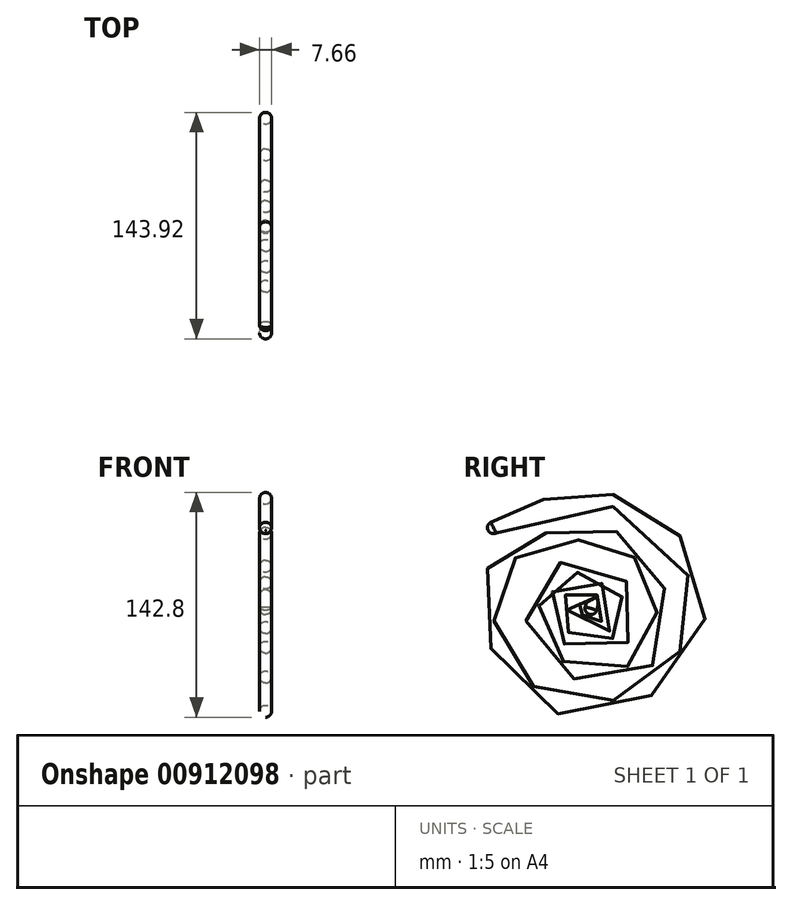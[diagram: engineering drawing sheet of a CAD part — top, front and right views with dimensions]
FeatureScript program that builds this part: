
annotation { "Feature Type Name" : "Feature", "Feature Type Description" : "" }
export const myFeature = defineFeature(function(context is Context, id is Id, definition is map)
    precondition{}
    {
        {
            var Q0;
            Q0=qCreatedBy(makeId("Right.planeOp"),FACE);
            var sketch = newSketch(context, id + "F0", { "sketchPlane" : qUnion([Q0])});
            skFitSpline(sketch, "E0", {"points": [v(-61.4, 46.77) * mm, v(-21.75, 63.7) * mm, v(40.37, 56.93) * mm, v(70.1, -19.46) * mm, v(-17.16, -65.63) * mm, v(-62.36, 11.24) * mm, v(-20.3, 42.18) * mm, v(33.84, 32.75) * mm, v(42.06, -34.45) * mm, v(-23.45, -33.72) * mm, v(-23.2, 18) * mm, v(23.45, 11.97) * mm, v(22, -23.8) * mm, v(-18.13, -15.83) * mm, v(-13.05, 10.27) * mm, v(11.36, 7.61) * mm, v(14.26, -13.42) * mm, v(-6.04, -7.61) * mm, v(-4.1, 4.71) * mm, v(3.87, 2.78) * mm, v(2.66, -6.4) * mm], "startDerivative": vector(711, 380.87) * mm, "endDerivative": vector(-170.53, -435.93) * mm});
            skSolve(sketch);
        }
        {
            var Q0;
            Q0=sQuery(id+"F0.wireOp",VERTEX,"E0.start");
            var Q1;
            Q1=sQuery(id+"F0.wireOp",EDGE,"E0");
            cPlane(context, id + "F1", {"entities" : qUnion([Q0, Q1]), "cplaneType" : CPlaneType.CURVE_POINT, "offset" : 25.4 * mm, "width" : 152.4 * mm, "height" : 152.4 * mm});
        }
        {
            var Q0;
            Q0=qCreatedBy(id+"F1.planeOp",FACE);
            var sketch = newSketch(context, id + "F2", { "sketchPlane" : qUnion([Q0])});
            skCircle(sketch, "E1", {"center": v(0, 70.22) * mm, "radius": 3.83 * mm});
            skSolve(sketch);
        }
        {
            var Q0;
            Q0=makeQuery(id+"F2.imprint","IMPRINT",FACE,{"disambiguationData":[TD([[makeQuery(id+"F2.imprint","IMPRINT",EDGE,{"derivedFrom":sQuery(id+"F2.wireOp",EDGE,"E1")}),1.0]])]});
            var Q1;
            Q1=sQuery(id+"F0.wireOp",EDGE,"E0");
            sweep(context, id + "F3", {"profiles" : qUnion([Q0]), "path" : qUnion([Q1])});
        }
        {
            var Q0;
            Q0=makeQuery(id+"F3.opSweep","CAP_EDGE",EDGE,{"disambiguationData":[OSD([sQuery(id+"F0.wireOp",VERTEX,"E0.start"),sQuery(id+"F2.wireOp",EDGE,"E1")])],"isStart":true});
            fillet(context, id + "F4", {"entities" : qUnion([Q0]), "radius" : 3.8 * mm, "tangentPropagation" : true, "allowEdgeOverflow" : false});
        }
        {
            var Q0;
            Q0=makeQuery(id+"F3.opSweep","CAP_EDGE",EDGE,{"disambiguationData":[OSD([sQuery(id+"F0.wireOp",VERTEX,"E0.end"),sQuery(id+"F2.wireOp",EDGE,"E1")])],"isStart":false});
            fillet(context, id + "F5", {"entities" : qUnion([Q0]), "radius" : 3.8 * mm, "tangentPropagation" : true, "allowEdgeOverflow" : false});
        }
    });
